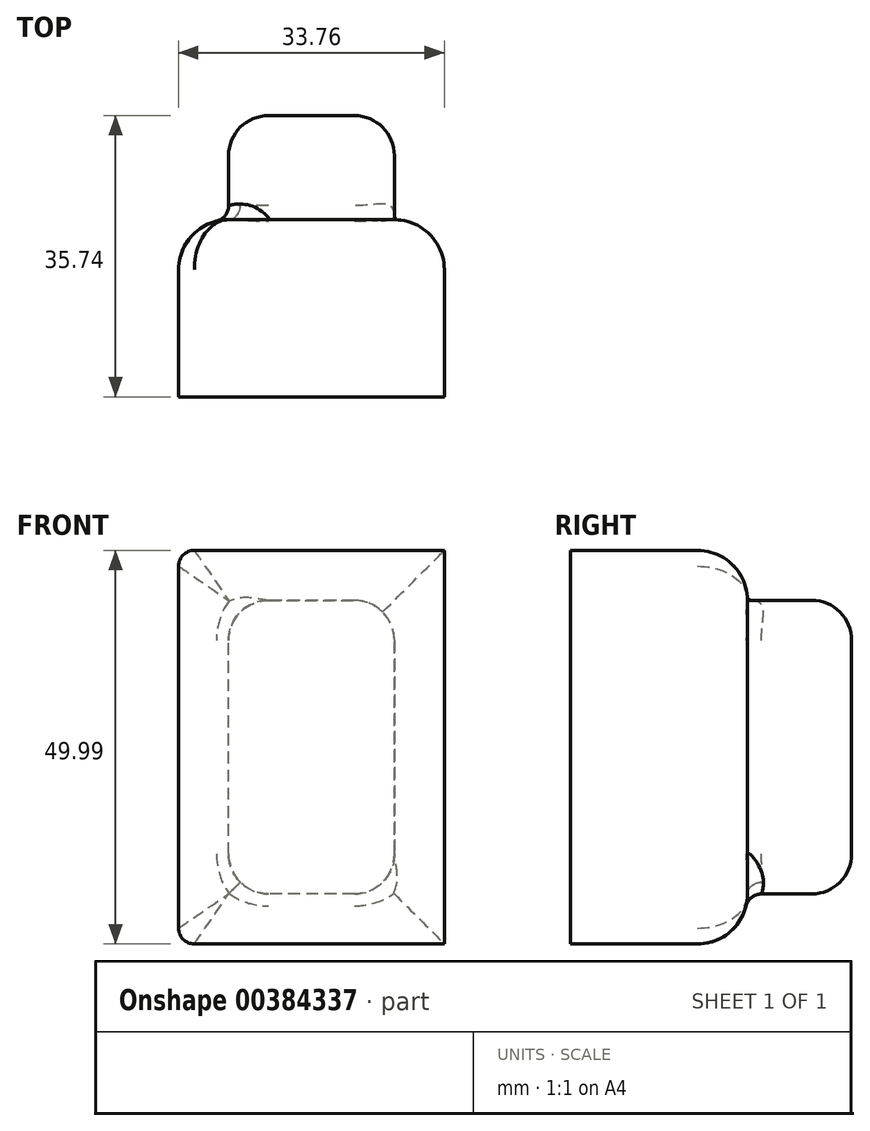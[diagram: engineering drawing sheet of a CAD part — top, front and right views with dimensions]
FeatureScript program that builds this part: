
annotation { "Feature Type Name" : "Feature", "Feature Type Description" : "" }
export const myFeature = defineFeature(function(context is Context, id is Id, definition is map)
    precondition{}
    {
        {
            var Q0;
            Q0=qCreatedBy(makeId("Front.planeOp"),FACE);
            var sketch = newSketch(context, id + "F0", { "sketchPlane" : qUnion([Q0])});
            skLineSegment(sketch, "E0.bottom", {"start": v(-9.32, 0) * mm, "end": v(-43.08, 0) * mm});
            skLineSegment(sketch, "E0.top", {"start": v(-9.32, 50) * mm, "end": v(-43.08, 50) * mm});
            skLineSegment(sketch, "E0.left", {"start": v(-9.32, 0) * mm, "end": v(-9.32, 50) * mm});
            skLineSegment(sketch, "E0.right", {"start": v(-43.08, 0) * mm, "end": v(-43.08, 50) * mm});
            skSolve(sketch);
        }
        {
            var Q0;
            Q0=makeQuery(id+"F0.imprint","IMPRINT",FACE,{"disambiguationData":[TD([[makeQuery(id+"F0.imprint","IMPRINT",EDGE,{"derivedFrom":sQuery(id+"F0.wireOp",EDGE,"E0.bottom")}),-1.0]])]});
            extrude(context, id + "F1", {"entities" : qUnion([Q0]), "oppositeDirection" : true, "depth" : 22.52 * mm});
        }
        {
            var Q0;
            Q0=makeQuery(id+"F1.opExtrude","CAP_EDGE",EDGE,{"disambiguationData":[OSD([sQuery(id+"F0.wireOp",EDGE,"E0.right")])],"isStart":false});
            var Q1;
            Q1=makeQuery(id+"F1.opExtrude","CAP_FACE",FACE,{"disambiguationData":[OSD([sQuery(id+"F0.wireOp",EDGE,"E0.bottom"),sQuery(id+"F0.wireOp",EDGE,"E0.top"),sQuery(id+"F0.wireOp",EDGE,"E0.left"),sQuery(id+"F0.wireOp",EDGE,"E0.right")])],"isStart":false});
            fillet(context, id + "F2", {"entities" : qUnion([Q0, Q1]), "radius" : 6.35 * mm, "tangentPropagation" : true, "allowEdgeOverflow" : false});
        }
        {
            var Q0;
            Q0=makeQuery(id+"F1.opExtrude","CAP_FACE",FACE,{"disambiguationData":[OSD([sQuery(id+"F0.wireOp",EDGE,"E0.bottom"),sQuery(id+"F0.wireOp",EDGE,"E0.top"),sQuery(id+"F0.wireOp",EDGE,"E0.left"),sQuery(id+"F0.wireOp",EDGE,"E0.right")])],"isStart":false});
            extrude(context, id + "F3", {"entities" : qUnion([Q0]), "operationType" : NewBodyOperationType.ADD, "depth" : 13.22 * mm});
        }
        {
            var Q0;
            {var subQ0=sQuery(id+"F0.wireOp",EDGE,"E0.right");var subQ1=sQuery(id+"F0.wireOp",EDGE,"E0.left");var subQ2=sQuery(id+"F0.wireOp",EDGE,"E0.top");var subQ3=sQuery(id+"F0.wireOp",EDGE,"E0.bottom");Q0=makeQuery(id+"F3.opExtrude","CAP_EDGE",EDGE,{"disambiguationData":[OSD([subQ3,subQ2,subQ1,subQ0]),TDD([makeQuery(id+"F2.opFillet","BLEND_EDGE",EDGE,{"blendedFrom":[makeQuery(id+"F1.opExtrude","CAP_EDGE",EDGE,{"disambiguationData":[OSD([subQ2])],"isStart":false}),makeQuery(id+"F1.opExtrude","CAP_FACE",FACE,{"disambiguationData":[OSD([subQ3,subQ2,subQ1,subQ0])],"isStart":false})],"blendedInto":[makeQuery(id+"F1.opExtrude","CAP_FACE",FACE,{"disambiguationData":[OSD([subQ3,subQ2,subQ1,subQ0])],"isStart":false})]})])],"isStart":false});}
            var Q1;
            Q1=makeQuery(id+"F3.opExtrude","CAP_FACE",FACE,{"disambiguationData":[OSD([sQuery(id+"F0.wireOp",EDGE,"E0.bottom"),sQuery(id+"F0.wireOp",EDGE,"E0.top"),sQuery(id+"F0.wireOp",EDGE,"E0.left"),sQuery(id+"F0.wireOp",EDGE,"E0.right")])],"isStart":false});
            fillet(context, id + "F4", {"entities" : qUnion([Q0, Q1]), "radius" : 5.08 * mm, "tangentPropagation" : true, "allowEdgeOverflow" : false});
        }
        {
            var Q0;
            {var subQ0=sQuery(id+"F0.wireOp",EDGE,"E0.right");var subQ1=sQuery(id+"F0.wireOp",EDGE,"E0.left");var subQ2=sQuery(id+"F0.wireOp",EDGE,"E0.top");var subQ3=sQuery(id+"F0.wireOp",EDGE,"E0.bottom");var subQ4=makeQuery(id+"F1.opExtrude","CAP_FACE",FACE,{"disambiguationData":[OSD([subQ3,subQ2,subQ1,subQ0])],"isStart":false});Q0=makeQuery(id+"F4.opFillet","BLEND_EDGE",EDGE,{"blendedFrom":[makeQuery(id+"F3.opExtrude","CAP_EDGE",EDGE,{"disambiguationData":[OSD([subQ3,subQ2,subQ1,subQ0]),TDD([makeQuery(id+"F2.opFillet","BLEND_EDGE",EDGE,{"blendedFrom":[makeQuery(id+"F1.opExtrude","CAP_EDGE",EDGE,{"disambiguationData":[OSD([subQ2])],"isStart":false}),subQ4],"blendedInto":[subQ4]})])],"isStart":false}),makeQuery(id+"F3.opExtrude","CAP_EDGE",EDGE,{"disambiguationData":[OSD([subQ3,subQ2,subQ1,subQ0]),TDD([makeQuery(id+"F2.opFillet","BLEND_EDGE",EDGE,{"blendedFrom":[makeQuery(id+"F1.opExtrude","CAP_EDGE",EDGE,{"disambiguationData":[OSD([subQ0])],"isStart":false}),subQ4],"blendedInto":[subQ4]})])],"isStart":false})],"blendedInto":[]});}
            var Q1;
            {var subQ0=sQuery(id+"F0.wireOp",EDGE,"E0.right");var subQ1=sQuery(id+"F0.wireOp",EDGE,"E0.left");var subQ2=sQuery(id+"F0.wireOp",EDGE,"E0.top");var subQ3=sQuery(id+"F0.wireOp",EDGE,"E0.bottom");Q1=makeQuery(id+"F3.opExtrude","SWEPT_EDGE",EDGE,{"disambiguationData":[OSD([subQ3,subQ2,subQ1,subQ0]),TDD([makeQuery(id+"F2.opFillet","BLEND_VERTEX",VERTEX,{"blendedFrom":[makeQuery(id+"F1.opExtrude","CAP_EDGE",EDGE,{"disambiguationData":[OSD([subQ2])],"isStart":false}),makeQuery(id+"F1.opExtrude","CAP_EDGE",EDGE,{"disambiguationData":[OSD([subQ1])],"isStart":false}),makeQuery(id+"F1.opExtrude","CAP_FACE",FACE,{"disambiguationData":[OSD([subQ3,subQ2,subQ1,subQ0])],"isStart":false})],"blendedInto":[makeQuery(id+"F1.opExtrude","CAP_FACE",FACE,{"disambiguationData":[OSD([subQ3,subQ2,subQ1,subQ0])],"isStart":false})]})])]});}
            var Q2;
            {var subQ0=sQuery(id+"F0.wireOp",EDGE,"E0.right");var subQ1=sQuery(id+"F0.wireOp",EDGE,"E0.left");var subQ2=sQuery(id+"F0.wireOp",EDGE,"E0.top");var subQ3=sQuery(id+"F0.wireOp",EDGE,"E0.bottom");Q2=makeQuery(id+"F3.opExtrude","SWEPT_EDGE",EDGE,{"disambiguationData":[OSD([subQ3,subQ2,subQ1,subQ0]),TDD([makeQuery(id+"F2.opFillet","BLEND_VERTEX",VERTEX,{"blendedFrom":[makeQuery(id+"F1.opExtrude","CAP_EDGE",EDGE,{"disambiguationData":[OSD([subQ3])],"isStart":false}),makeQuery(id+"F1.opExtrude","CAP_EDGE",EDGE,{"disambiguationData":[OSD([subQ1])],"isStart":false}),makeQuery(id+"F1.opExtrude","CAP_FACE",FACE,{"disambiguationData":[OSD([subQ3,subQ2,subQ1,subQ0])],"isStart":false})],"blendedInto":[makeQuery(id+"F1.opExtrude","CAP_FACE",FACE,{"disambiguationData":[OSD([subQ3,subQ2,subQ1,subQ0])],"isStart":false})]})])]});}
            var Q3;
            {var subQ0=sQuery(id+"F0.wireOp",EDGE,"E0.right");var subQ1=sQuery(id+"F0.wireOp",EDGE,"E0.left");var subQ2=sQuery(id+"F0.wireOp",EDGE,"E0.top");var subQ3=sQuery(id+"F0.wireOp",EDGE,"E0.bottom");Q3=makeQuery(id+"F3.opExtrude","SWEPT_EDGE",EDGE,{"disambiguationData":[OSD([subQ3,subQ2,subQ1,subQ0]),TDD([makeQuery(id+"F2.opFillet","BLEND_VERTEX",VERTEX,{"blendedFrom":[makeQuery(id+"F1.opExtrude","CAP_EDGE",EDGE,{"disambiguationData":[OSD([subQ2])],"isStart":false}),makeQuery(id+"F1.opExtrude","CAP_EDGE",EDGE,{"disambiguationData":[OSD([subQ0])],"isStart":false}),makeQuery(id+"F1.opExtrude","CAP_FACE",FACE,{"disambiguationData":[OSD([subQ3,subQ2,subQ1,subQ0])],"isStart":false})],"blendedInto":[makeQuery(id+"F1.opExtrude","CAP_FACE",FACE,{"disambiguationData":[OSD([subQ3,subQ2,subQ1,subQ0])],"isStart":false})]})])]});}
            var Q4;
            {var subQ0=sQuery(id+"F0.wireOp",EDGE,"E0.right");var subQ1=sQuery(id+"F0.wireOp",EDGE,"E0.left");var subQ2=sQuery(id+"F0.wireOp",EDGE,"E0.top");var subQ3=sQuery(id+"F0.wireOp",EDGE,"E0.bottom");Q4=makeQuery(id+"F3.opExtrude","SWEPT_EDGE",EDGE,{"disambiguationData":[OSD([subQ3,subQ2,subQ1,subQ0]),TDD([makeQuery(id+"F2.opFillet","BLEND_VERTEX",VERTEX,{"blendedFrom":[makeQuery(id+"F1.opExtrude","CAP_EDGE",EDGE,{"disambiguationData":[OSD([subQ3])],"isStart":false}),makeQuery(id+"F1.opExtrude","CAP_EDGE",EDGE,{"disambiguationData":[OSD([subQ0])],"isStart":false}),makeQuery(id+"F1.opExtrude","CAP_FACE",FACE,{"disambiguationData":[OSD([subQ3,subQ2,subQ1,subQ0])],"isStart":false})],"blendedInto":[makeQuery(id+"F1.opExtrude","CAP_FACE",FACE,{"disambiguationData":[OSD([subQ3,subQ2,subQ1,subQ0])],"isStart":false})]})])]});}
            fillet(context, id + "F5", {"entities" : qUnion([Q0, Q1, Q2, Q3, Q4]), "radius" : 5.08 * mm, "tangentPropagation" : true, "allowEdgeOverflow" : false});
        }
        {
            var Q0;
            Q0=makeQuery(id+"F1.opExtrude","SWEPT_EDGE",EDGE,{"disambiguationData":[OSD([sQuery(id+"F0.wireOp",EDGE,"E0.bottom"),sQuery(id+"F0.wireOp",EDGE,"E0.right")])]});
            var Q1;
            {var subQ0=sQuery(id+"F0.wireOp",EDGE,"E0.right");var subQ1=sQuery(id+"F0.wireOp",EDGE,"E0.left");var subQ2=sQuery(id+"F0.wireOp",EDGE,"E0.top");var subQ3=sQuery(id+"F0.wireOp",EDGE,"E0.bottom");Q1=makeQuery(id+"F5.opFillet","BLEND_FACE",FACE,{"disambiguationData":[OSD([subQ3,subQ2,subQ1,subQ0]),TDD([makeQuery(id+"F3.opExtrude","SWEPT_EDGE",EDGE,{"disambiguationData":[OSD([subQ3,subQ2,subQ1,subQ0]),TDD([makeQuery(id+"F2.opFillet","BLEND_VERTEX",VERTEX,{"blendedFrom":[makeQuery(id+"F1.opExtrude","CAP_EDGE",EDGE,{"disambiguationData":[OSD([subQ3])],"isStart":false}),makeQuery(id+"F1.opExtrude","CAP_EDGE",EDGE,{"disambiguationData":[OSD([subQ0])],"isStart":false}),makeQuery(id+"F1.opExtrude","CAP_FACE",FACE,{"disambiguationData":[OSD([subQ3,subQ2,subQ1,subQ0])],"isStart":false})],"blendedInto":[makeQuery(id+"F1.opExtrude","CAP_FACE",FACE,{"disambiguationData":[OSD([subQ3,subQ2,subQ1,subQ0])],"isStart":false})]})])]})])]});}
            var Q2;
            Q2=makeQuery(id+"F2.opFillet","BLEND_FACE",FACE,{"disambiguationData":[OSD([sQuery(id+"F0.wireOp",EDGE,"E0.right")])]});
            fillet(context, id + "F6", {"entities" : qUnion([Q0, Q1, Q2]), "radius" : 2 * mm, "tangentPropagation" : true, "allowEdgeOverflow" : false});
        }
    });
